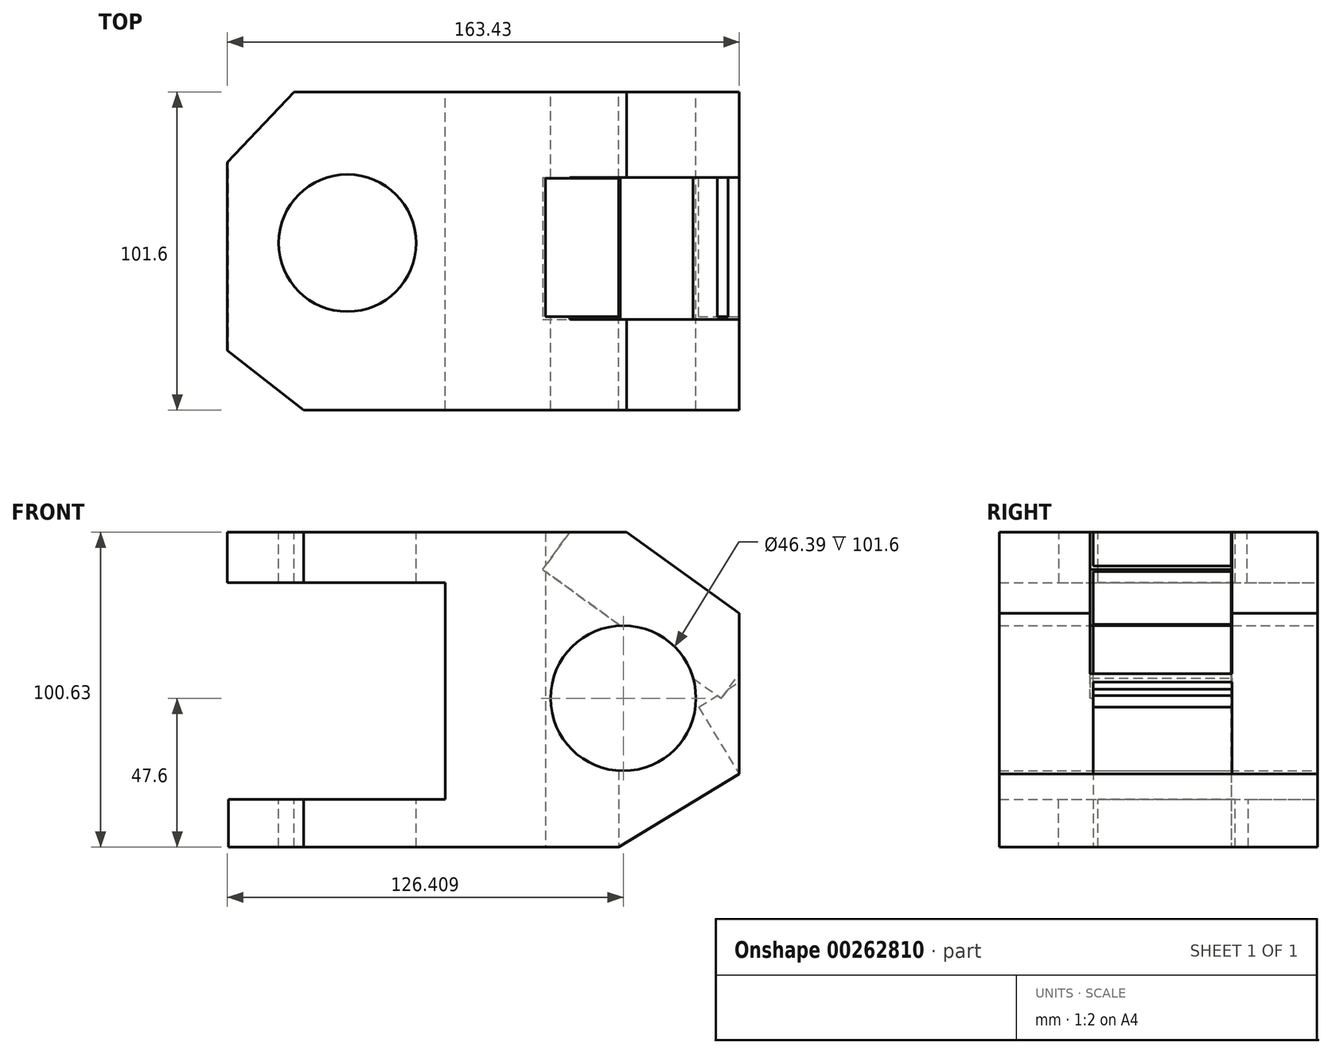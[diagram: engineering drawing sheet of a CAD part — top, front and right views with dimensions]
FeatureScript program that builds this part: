
annotation { "Feature Type Name" : "Feature", "Feature Type Description" : "" }
export const myFeature = defineFeature(function(context is Context, id is Id, definition is map)
    precondition{}
    {
        {
            var Q0;
            Q0=qCreatedBy(makeId("Front.planeOp"),FACE);
            var sketch = newSketch(context, id + "F0", { "sketchPlane" : qUnion([Q0])});
            skLineSegment(sketch, "E0", {"start": v(-66.8, 53.03) * mm, "end": v(40.18, 53.03) * mm});
            skLineSegment(sketch, "E1", {"start": v(40.18, 53.03) * mm, "end": v(76.1, 27.08) * mm});
            skLineSegment(sketch, "E2", {"start": v(76.1, 27.08) * mm, "end": v(76.1, -24.18) * mm});
            skLineSegment(sketch, "E3", {"start": v(76.1, -24.18) * mm, "end": v(37.65, -47.6) * mm});
            skLineSegment(sketch, "E4", {"start": v(37.65, -47.6) * mm, "end": v(-67.88, -47.6) * mm});
            skLineSegment(sketch, "E5", {"start": v(-67.88, -47.6) * mm, "end": v(-67.88, -32.25) * mm});
            skLineSegment(sketch, "E6", {"start": v(-67.88, -32.25) * mm, "end": v(-17.75, -32.25) * mm});
            skLineSegment(sketch, "E7", {"start": v(-17.75, -32.25) * mm, "end": v(-17.75, 36.9) * mm});
            skLineSegment(sketch, "E8", {"start": v(-17.75, 36.9) * mm, "end": v(-66.8, 36.9) * mm});
            skLineSegment(sketch, "E9", {"start": v(-66.8, 36.9) * mm, "end": v(-66.8, 53.03) * mm});
            skCircle(sketch, "E10", {"center": v(39.07, 0) * mm, "radius": 23.2 * mm});
            skLineSegment(sketch, "E11", {"start": v(-67.88, -47.6) * mm, "end": v(-87.03, -47.6) * mm});
            skLineSegment(sketch, "E12", {"start": v(-87.03, -47.6) * mm, "end": v(-87.03, -32.25) * mm});
            skLineSegment(sketch, "E13", {"start": v(-87.03, -32.25) * mm, "end": v(-67.88, -32.25) * mm});
            skLineSegment(sketch, "E14", {"start": v(-66.8, 53.03) * mm, "end": v(-87.34, 53.03) * mm});
            skLineSegment(sketch, "E15", {"start": v(-87.34, 53.03) * mm, "end": v(-87.34, 36.9) * mm});
            skLineSegment(sketch, "E16", {"start": v(-87.34, 36.9) * mm, "end": v(-66.8, 36.9) * mm});
            skSolve(sketch);
        }
        {
            var Q0;
            Q0 = qSketchRegion(id + "F0", true);
            extrude(context, id + "F1", {"entities" : qUnion([Q0]), "depth" : 101.6 * mm});
        }
        {
            var Q0;
            Q0=makeQuery(id+"F1.opExtrude","SWEPT_FACE",FACE,{"disambiguationData":[OSD([sQuery(id+"F0.wireOp",EDGE,"E0"),sQuery(id+"F0.wireOp",EDGE,"E14")])]});
            var sketch = newSketch(context, id + "F2", { "sketchPlane" : qUnion([Q0])});
            skLineSegment(sketch, "E17", {"start": v(-87.34, -22.5) * mm, "end": v(-66.1, 0) * mm});
            skLineSegment(sketch, "E18", {"start": v(-66.1, 0) * mm, "end": v(-87.34, 0) * mm});
            skLineSegment(sketch, "E19", {"start": v(-87.34, 0) * mm, "end": v(-87.34, -22.5) * mm});
            skLineSegment(sketch, "E20", {"start": v(-87.34, -101.6) * mm, "end": v(-63.06, -101.6) * mm});
            skLineSegment(sketch, "E21", {"start": v(-63.06, -101.6) * mm, "end": v(-87.34, -82.57) * mm});
            skLineSegment(sketch, "E22", {"start": v(-87.34, -82.57) * mm, "end": v(-87.34, -101.6) * mm});
            skSolve(sketch);
        }
        {
            var Q0;
            Q0=makeQuery(id+"F2.imprint","IMPRINT",FACE,{"disambiguationData":[TD([[makeQuery(id+"F2.imprint","IMPRINT",EDGE,{"derivedFrom":sQuery(id+"F2.wireOp",EDGE,"E17")}),1.0]])]});
            var Q1;
            Q1=makeQuery(id+"F2.imprint","IMPRINT",FACE,{"disambiguationData":[TD([[makeQuery(id+"F2.imprint","IMPRINT",EDGE,{"derivedFrom":sQuery(id+"F2.wireOp",EDGE,"E17")}),1.0]])]});
            var Q2;
            Q2=makeQuery(id+"F2.imprint","IMPRINT",FACE,{"disambiguationData":[TD([[makeQuery(id+"F2.imprint","IMPRINT",EDGE,{"derivedFrom":sQuery(id+"F2.wireOp",EDGE,"E20")}),-1.0]])]});
            extrude(context, id + "F3", {"entities" : qUnion([Q0, Q1, Q2]), "operationType" : NewBodyOperationType.REMOVE, "oppositeDirection" : true, "depth" : 152.4 * mm});
        }
        {
            var Q0;
            Q0=makeQuery(id+"F1.opExtrude","SWEPT_FACE",FACE,{"disambiguationData":[OSD([sQuery(id+"F0.wireOp",EDGE,"E0"),sQuery(id+"F0.wireOp",EDGE,"E14")])]});
            var sketch = newSketch(context, id + "F4", { "sketchPlane" : qUnion([Q0])});
            skCircle(sketch, "E23", {"center": v(-49.03, -48.23) * mm, "radius": 21.92 * mm});
            skSolve(sketch);
        }
        {
            var Q0;
            Q0=makeQuery(id+"F4.imprint","IMPRINT",FACE,{"disambiguationData":[TD([[makeQuery(id+"F4.imprint","IMPRINT",EDGE,{"derivedFrom":sQuery(id+"F4.wireOp",EDGE,"E23")}),1.0]])]});
            extrude(context, id + "F5", {"entities" : qUnion([Q0]), "operationType" : NewBodyOperationType.REMOVE, "oppositeDirection" : true, "depth" : 254 * mm});
        }
        {
            var Q0;
            Q0=makeQuery(id+"F1.opExtrude","SWEPT_FACE",FACE,{"disambiguationData":[OSD([sQuery(id+"F0.wireOp",EDGE,"E1")])]});
            var sketch = newSketch(context, id + "F6", { "sketchPlane" : qUnion([Q0])});
            skLineSegment(sketch, "E24.bottom", {"start": v(-13.25, -27.34) * mm, "end": v(57.08, -27.34) * mm});
            skLineSegment(sketch, "E24.top", {"start": v(-13.25, -72.64) * mm, "end": v(57.08, -72.64) * mm});
            skLineSegment(sketch, "E24.left", {"start": v(-13.25, -27.34) * mm, "end": v(-13.25, -72.64) * mm});
            skLineSegment(sketch, "E24.right", {"start": v(57.08, -27.34) * mm, "end": v(57.08, -72.64) * mm});
            skSolve(sketch);
        }
        {
            var Q0;
            Q0 = qSketchRegion(id + "F6", true);
            extrude(context, id + "F7", {"entities" : qUnion([Q0]), "operationType" : NewBodyOperationType.REMOVE, "oppositeDirection" : true, "depth" : 25.4 * mm});
        }
        {
            var Q0;
            Q0=makeQuery(id+"F1.opExtrude","SWEPT_FACE",FACE,{"disambiguationData":[OSD([sQuery(id+"F0.wireOp",EDGE,"E4"),sQuery(id+"F0.wireOp",EDGE,"E11")])]});
            var sketch = newSketch(context, id + "F8", { "sketchPlane" : qUnion([Q0])});
            skLineSegment(sketch, "E25.bottom", {"start": v(14.19, 71.72) * mm, "end": v(37.65, 71.72) * mm});
            skLineSegment(sketch, "E25.top", {"start": v(14.19, 27.55) * mm, "end": v(37.65, 27.55) * mm});
            skLineSegment(sketch, "E25.left", {"start": v(14.19, 71.72) * mm, "end": v(14.19, 27.55) * mm});
            skLineSegment(sketch, "E25.right", {"start": v(37.65, 71.72) * mm, "end": v(37.65, 27.55) * mm});
            skSolve(sketch);
        }
        {
            var Q0;
            Q0=makeQuery(id+"F8.imprint","IMPRINT",FACE,{"disambiguationData":[TD([[makeQuery(id+"F8.imprint","IMPRINT",EDGE,{"derivedFrom":sQuery(id+"F8.wireOp",EDGE,"E25.bottom")}),-1.0]])]});
            extrude(context, id + "F9", {"entities" : qUnion([Q0]), "operationType" : NewBodyOperationType.REMOVE, "oppositeDirection" : true, "depth" : 254 * mm});
        }
        {
            var Q0;
            Q0=makeQuery(id+"F1.opExtrude","SWEPT_FACE",FACE,{"disambiguationData":[OSD([sQuery(id+"F0.wireOp",EDGE,"E3")])]});
            var sketch = newSketch(context, id + "F10", { "sketchPlane" : qUnion([Q0])});
            skLineSegment(sketch, "E26.bottom", {"start": v(7.4, 71.72) * mm, "end": v(69.16, 71.72) * mm});
            skLineSegment(sketch, "E26.top", {"start": v(7.4, 27.36) * mm, "end": v(69.16, 27.36) * mm});
            skLineSegment(sketch, "E26.left", {"start": v(7.4, 71.72) * mm, "end": v(7.4, 27.36) * mm});
            skLineSegment(sketch, "E26.right", {"start": v(69.16, 71.72) * mm, "end": v(69.16, 27.36) * mm});
            skSolve(sketch);
        }
        {
            var Q0;
            {var subQ0=sQuery(id+"F10.wireOp",EDGE,"E26.right");Q0=makeQuery(id+"F10.imprint","IMPRINT",FACE,{"disambiguationData":[TD([[makeQuery(id+"F10.imprint","IMPRINT",EDGE,{"derivedFrom":subQ0}),-1.0]])]});}
            extrude(context, id + "F11", {"entities" : qUnion([Q0]), "operationType" : NewBodyOperationType.REMOVE, "oppositeDirection" : true, "depth" : 25 * mm});
        }
    });
